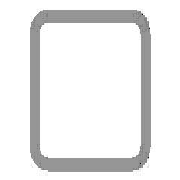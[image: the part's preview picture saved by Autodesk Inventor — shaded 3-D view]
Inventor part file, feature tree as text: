
AUTODESK INVENTOR PART (.ipt)
format: ipt  version: 2023 (Build 270158000, 158)  size: 214,016 bytes
history: native  units: mm (DEFAULTED — no unit token found)
features: other x18, sketch x5, extrude x3, plane x1
ambient origin geometry x8: Origin, YZ Plane, XZ Plane, XY Plane, X Axis, Y Axis, Z Axis, Center Point
bodies: Solid1 (feature_tree)
feature tree (27):
  parser-record x1  (decoder bookkeeping rows leaked as tree rows — omitted from the tree; the rows remain in map.json)
  other  "Driven Length"
  other  "Płaszczyzna początkowa"
  other  "Płaszczyzna końcowa"
  extrude  "Bryła"  TaperAngle=0.0deg  [1 undecoded]
  other  "Płaszczyzna konstrukcyjna4"
  other  "Podział1"
  other  "Płaszczyzna konstrukcyjna5"
  other  "Podział2"
  other  "Płaszczyzna konstrukcyjna6"
  other  "Płaszczyzna konstrukcyjna7"
  other  "Płaszczyzna konstrukcyjna8"
  extrude  "Wyciągnięcie proste2"  Depth=4.0mm
  other  "Utwórz kombinację1"
  other  "Płaszczyzna konstrukcyjna9"
  other  "Płaszczyzna konstrukcyjna10"
  other  "Płaszczyzna konstrukcyjna11"
  extrude  "Wyciągnięcie proste3"  Depth=4.0mm
  other  "Utwórz kombinację2"
  sketch  "Szkic"
  sketch  "Sketch3"  dims[d3=1540.0mm d4=0.0mm]
  plane  "Work Plane3"
  sketch  "Sketch4"  dims[d7=4.0mm d10=40.0mm d11=40.0mm d12=3.2mm d13=-20.0mm d14=1520.0mm d15=20.0mm d16=20.0mm d17=90.0deg d18=1540.0mm d19=0.13mm d20=0.0mm d21=0.13mm d22=0.0mm]
  sketch  "Szkic5"
  other  "Bryła2"
  sketch  "Szkic6"
  other  "Bryła3"
note: 1 required parameter value undecoded (feature->parameter linkage not recoverable at this tier; creation-order binding heuristic only, values carry confidence <= 0.55)
